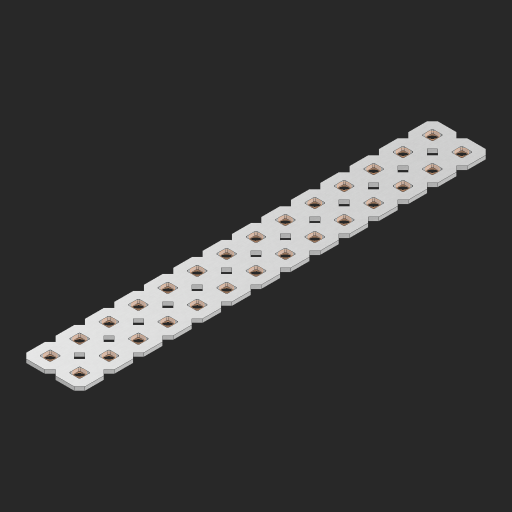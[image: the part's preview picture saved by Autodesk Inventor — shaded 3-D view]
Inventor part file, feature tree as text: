
AUTODESK INVENTOR PART (.ipt)
format: ipt  version: 2023 (Build 270158000, 158)  size: 595,968 bytes
history: native  units: in
note: dims shown in document units (in); Inventor stores cm internally (conversion verified against a paired STEP export)
features: other x29, extrude x27, sketch x2, pattern_linear x1
ambient origin geometry x8: Origin, YZ Plane, XZ Plane, XY Plane, X Axis, Y Axis, Z Axis, Center Point
bodies: Solid1 (feature_tree), Body (feature_tree)
feature tree (59):
  pattern_linear  "Rectangular Pattern1"  Spacing1=0.09in  [1 undecoded]
  sketch  "Sketch1"  dims[d1=0.5in]
  sketch  "Sketch2"  dims[d2=0.182in d3=0.09in d4=0.09in d5=0.09in d6=0.09in d7=0.09in d8=0.09in d9=0.09in d10=0.09in d11=0.02in d13=0.0in d14=0.172in d15=0.0625in d16=0.0in d19=0.5in d22=0.5in]
  other  "Srf1"
  other  "Srf126"
  other  "Srf127"
  other  "Srf128"
  other  "Srf129"
  other  "Srf130"
  other  "Srf131"
  other  "Srf250"
  other  "Srf251"
  other  "Srf252"
  other  "Srf253"
  other  "Srf254"
  other  "Srf255"
  other  "Srf256"
  other  "Srf268"
  other  "Srf269"
  other  "Srf270"
  other  "Srf271"
  other  "Srf272"
  other  "Srf273"
  other  "Srf274"
  other  "Srf275"
  other  "Srf276"
  other  "Srf277"
  other  "Srf278"
  other  "Srf279"
  other  "Srf280"
  other  "Srf281"
  other  "Circle"
  extrude  "ExtrusionSrf126"  Depth=0.09in
  extrude  "ExtrusionSrf127"  Depth=0.09in
  extrude  "ExtrusionSrf128"  Depth=0.09in
  extrude  "ExtrusionSrf129"  Depth=0.09in
  extrude  "ExtrusionSrf130"  Depth=0.09in
  extrude  "ExtrusionSrf131"  Depth=0.09in
  extrude  "ExtrusionSrf250"  Depth=0.09in
  extrude  "ExtrusionSrf251"  Depth=0.02in
  extrude  "ExtrusionSrf252"  TaperAngle=0.0deg  [1 undecoded]
  extrude  "ExtrusionSrf253"  Depth=0.5in
  extrude  "ExtrusionSrf254"  Depth=0.0625in TaperAngle=0.0deg
  extrude  "ExtrusionSrf255"  Depth=0.5in
  extrude  "ExtrusionSrf256"  Depth=0.5in
  extrude  "ExtrusionSrf268"  [1 undecoded]
  extrude  "ExtrusionSrf269"  [1 undecoded]
  extrude  "ExtrusionSrf270"  [1 undecoded]
  extrude  "ExtrusionSrf271"  [1 undecoded]
  extrude  "ExtrusionSrf272"  [1 undecoded]
  extrude  "ExtrusionSrf273"  [1 undecoded]
  extrude  "ExtrusionSrf274"  [1 undecoded]
  extrude  "ExtrusionSrf275"  [1 undecoded]
  extrude  "ExtrusionSrf276"  [1 undecoded]
  extrude  "ExtrusionSrf277"  [1 undecoded]
  extrude  "ExtrusionSrf278"  [1 undecoded]
  extrude  "ExtrusionSrf279"  [1 undecoded]
  extrude  "ExtrusionSrf280"  [1 undecoded]
  extrude  "ExtrusionSrf281"  [1 undecoded]
note: 16 required parameter values undecoded (feature->parameter linkage not recoverable at this tier; creation-order binding heuristic only, values carry confidence <= 0.55)
